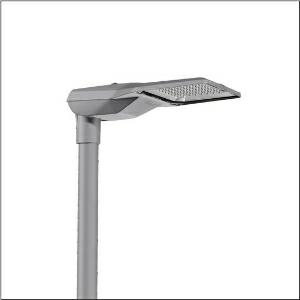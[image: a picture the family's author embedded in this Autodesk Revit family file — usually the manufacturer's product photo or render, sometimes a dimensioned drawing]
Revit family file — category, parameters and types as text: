
# Revit family: streetlight_sl_21_midi___st1_0a_5xe3d33s08nb_54c0
name_source: partatom
category: Lighting Fixtures
units: mm (PartAtom-declared; Revit-internal decimal feet)

## family parameters
Cut with Voids When Loaded = No
Host = Face
Light Source = No
Part Type = Normal
Room Calculation Point = No
Round Connector Dimension = Use Diameter
Shared = No

## types (1)
- --- (1 x LED, 22700 lm, 151.2 W, 3000K)
    Apparent Load = 151 VA
    CIE Flux Codes = 40 73 97 100 100
    Color Rendering = 70
    Color Temperature = 3000K
    Default Elevation = 1800 mm
    Description = Streetlight SL 21 midi, mast luminaire, primary light control with lens, of PMMA, primary optical cover: cover, of toughened safety glass, transparent, light distribution: ST1.0a, light emission: direct distribution, primary light characteristic: asymmetric, installation type: side-entry, post-top, LED, High Power LED, rated luminous flux: 22.700lm, luminous efficacy: 150lm/W, light colour: 730, colour temperature: 3000K, control gear: D4i, control: flexible luminous flux parameterisation, time-dependent luminous flux control, constant luminous flux control, overheat protection, pre-setting: logarithmic dimming characteristic, mains connection: 230..240V, AC, 50/60Hz, start of lifetime: 151W, end of service life: 157W, reduction: 70W, luminaire housing, of diecast aluminium, powder-coated, SITECO metallic grey (DB 702S), corrosivity category C5 high according to DIN EN ISO 12944, please order mast flange separately, inclination adjustable: 0°, 5°, 10°, 15°, sealing non-destructively replaceable, multi-level sealing system, length: 644mm, width: 335mm, height: 110mm, mast flange for spigot size: 42mm (side-entry): 5XC10008XM4, 60/48mm (side-entry/post-top): 5XC10108XM2, 76/60mm (side-entry/post-top): 5XC10108XM1, mounting height: 4..8m, Smart Interface above, protection rating (complete): IP66, insulation class (complete): insulation class II (safety insulation), certification: CE, ENEC, ENEC+, VDE, impact resistance: IK10, permissible operating ambient temperature for outdoor applications: -40..+50°C, standard-compliant lighting for roads and squares, packaging unit: 1 piece

Light Distribution: ST1.0a
    Height = 111 mm
    Lamp = 1 x LED
    Lamp Light Flux = 22700 lm
    Lamp Power = 151.2 W
    Lamp count = 1
    Length = 644 mm
    Luminous efficacy = 150 lm/W
    Manufacturer = Siteco
    ModVariant = No
    Model = 5XE3D33S08NB
    Number of Poles = 1
    OnlyDefault = Yes
    Power Factor = 1
    Product Name = Streetlight SL 21 midi | ST1.0a
    Product group = mast luminaire | pylon top
    ProductGroupID = 6100
    Protection Class = Protection class II
    Protection Degree = IP 66
    RLX_Detail_Level = 1
    RLX_Emergency_Light_Flux = 0 lm
    RLX_Emergency_Type = 0
    RLX_Emergency_Type_DB = No
    RlxData = <blob elided: 26965 chars, md5=ac19364d>
    Socket = socket
    Standby Power = 0 W
    System Light Flux = 22700 lm
    System Power = 151 W
    Type Comments = factory setting: luminous flux: 100 % | dim-lin: 254 | 802 mA
    Type Image = l_1004302.jpg
    URL = http://relux.com
    VarID = @adj_170091
    Voltage = 0 V
    Weight = 0.00 kg
    Width = 336 mm

## geometry (parser evidence)
native form markers: Blend x4, Sweep x11
no freeform markers — native parametric forms only
